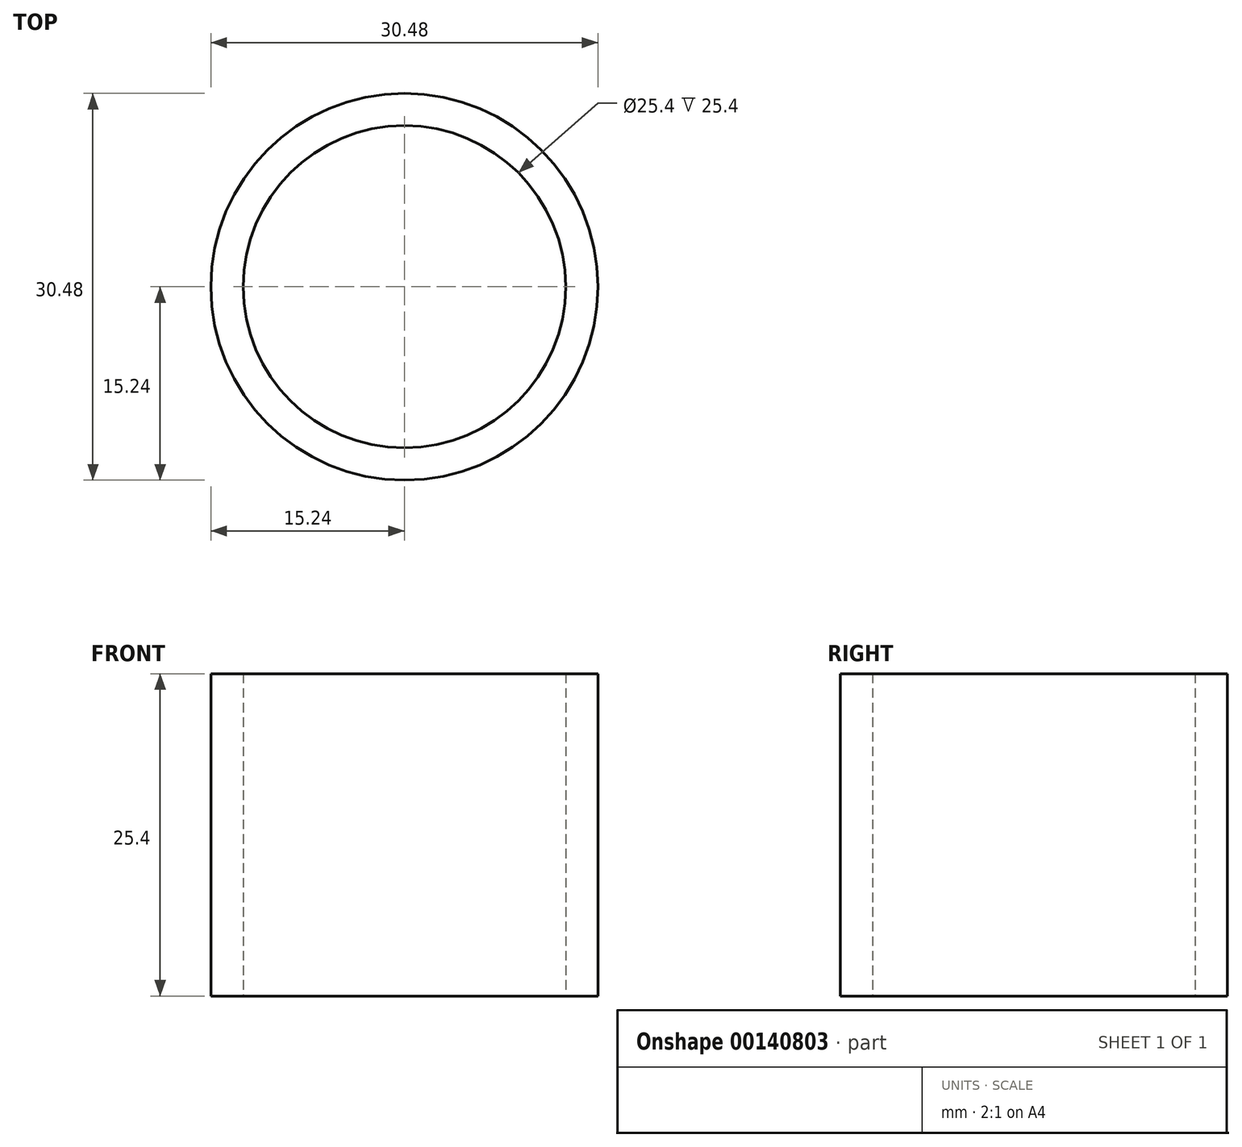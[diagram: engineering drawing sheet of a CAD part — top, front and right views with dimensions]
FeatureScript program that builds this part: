
annotation { "Feature Type Name" : "Feature", "Feature Type Description" : "" }
export const myFeature = defineFeature(function(context is Context, id is Id, definition is map)
    precondition{}
    {
        {
            var Q0;
            Q0=qCreatedBy(makeId("Top.planeOp"),FACE);
            var sketch = newSketch(context, id + "F0", { "sketchPlane" : qUnion([Q0])});
            skCircle(sketch, "E0", {"center": v(0, 0) * mm, "radius": 12.7 * mm});
            skCircle(sketch, "E1", {"center": v(0, 0) * mm, "radius": 15.24 * mm});
            skSolve(sketch);
        }
        {
            var Q0;
            Q0 = qSketchRegion(id + "F0", true);
            extrude(context, id + "F1", {"entities" : qUnion([Q0]), "depth" : 25.4 * mm});
        }
    });
